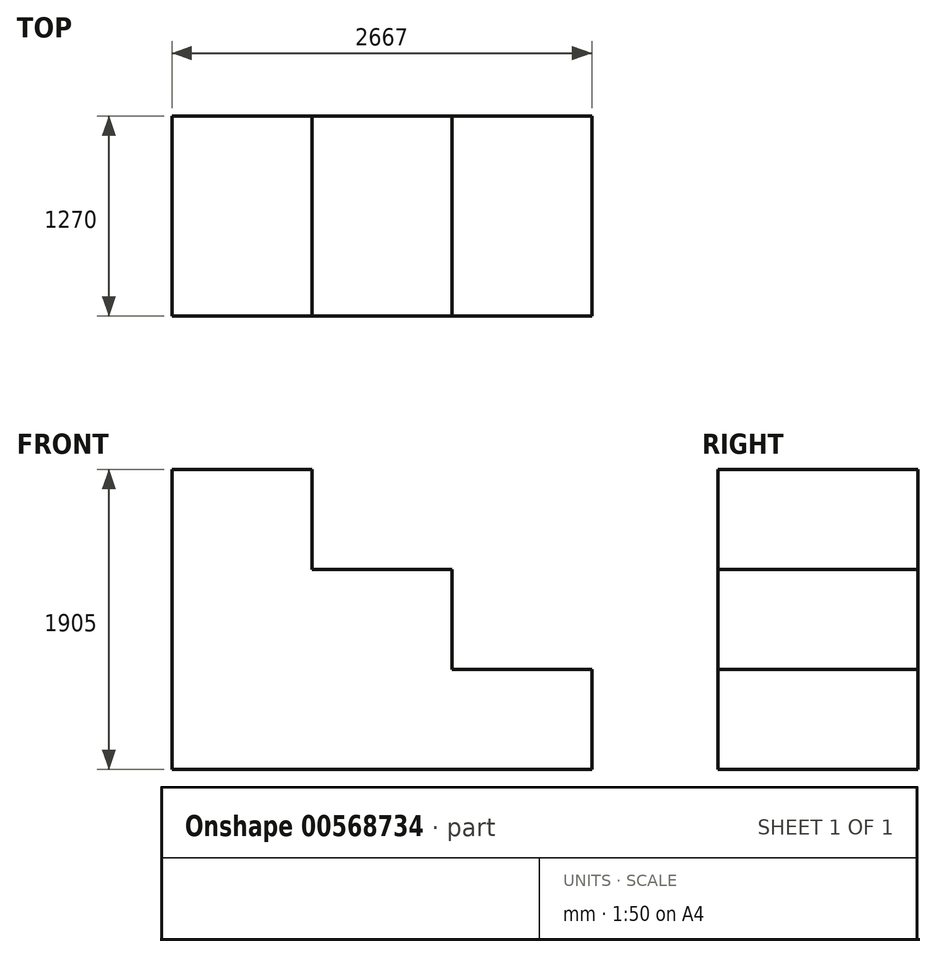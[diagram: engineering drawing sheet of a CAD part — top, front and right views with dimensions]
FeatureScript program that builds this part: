
annotation { "Feature Type Name" : "Feature", "Feature Type Description" : "" }
export const myFeature = defineFeature(function(context is Context, id is Id, definition is map)
    precondition{}
    {
        {
            var Q0;
            Q0=qCreatedBy(makeId("Front.planeOp"),FACE);
            var sketch = newSketch(context, id + "F0", { "sketchPlane" : qUnion([Q0])});
            skLineSegment(sketch, "E0.bottom", {"start": v(0, 0) * mm, "end": v(2667, 0) * mm});
            skLineSegment(sketch, "E0.top", {"start": v(0, 1905) * mm, "end": v(2667, 1905) * mm});
            skLineSegment(sketch, "E0.left", {"start": v(0, 0) * mm, "end": v(0, 1905) * mm});
            skLineSegment(sketch, "E0.right", {"start": v(2667, 0) * mm, "end": v(2667, 1905) * mm});
            skSolve(sketch);
        }
        {
            var Q0;
            Q0 = qSketchRegion(id + "F0", true);
            var Q1;
            Q1=makeQuery(id+"F0.imprint","IMPRINT",FACE,{"disambiguationData":[TD([[makeQuery(id+"F0.imprint","IMPRINT",EDGE,{"derivedFrom":sQuery(id+"F0.wireOp",EDGE,"E0.bottom")}),1.0]])]});
            extrude(context, id + "F1", {"entities" : qUnion([Q0, Q1]), "depth" : 1270 * mm, "offsetDistance" : 25.4 * mm});
        }
        {
            var Q0;
            Q0=makeQuery(id+"F1.opExtrude","CAP_FACE",FACE,{"disambiguationData":[OSD([sQuery(id+"F0.wireOp",EDGE,"E0.bottom"),sQuery(id+"F0.wireOp",EDGE,"E0.top"),sQuery(id+"F0.wireOp",EDGE,"E0.left"),sQuery(id+"F0.wireOp",EDGE,"E0.right")])],"isStart":true});
            var sketch = newSketch(context, id + "F2", { "sketchPlane" : qUnion([Q0])});
            skLineSegment(sketch, "E1", {"start": v(-2667, 0) * mm, "end": v(-2667, 635) * mm});
            skLineSegment(sketch, "E2", {"start": v(-2667, 635) * mm, "end": v(-1778, 635) * mm});
            skLineSegment(sketch, "E3", {"start": v(-1778, 635) * mm, "end": v(-1778, 1270) * mm});
            skLineSegment(sketch, "E4", {"start": v(-1778, 1270) * mm, "end": v(-889, 1270) * mm});
            skLineSegment(sketch, "E5", {"start": v(-889, 1270) * mm, "end": v(-889, 1905) * mm});
            skLineSegment(sketch, "E6", {"start": v(-889, 1905) * mm, "end": v(-2667, 1905) * mm});
            skLineSegment(sketch, "E7", {"start": v(-2667, 1905) * mm, "end": v(-2667, 635) * mm});
            skSolve(sketch);
        }
        {
            var Q0;
            Q0=makeQuery(id+"F2.imprint","IMPRINT",FACE,{"disambiguationData":[TD([[makeQuery(id+"F2.imprint","IMPRINT",EDGE,{"derivedFrom":sQuery(id+"F2.wireOp",EDGE,"E2")}),1.0]])]});
            extrude(context, id + "F3", {"entities" : qUnion([Q0]), "operationType" : NewBodyOperationType.REMOVE, "endBound" : BoundingType.THROUGH_ALL, "oppositeDirection" : true, "depth" : 25.4 * mm, "offsetDistance" : 25.4 * mm});
        }
    });
